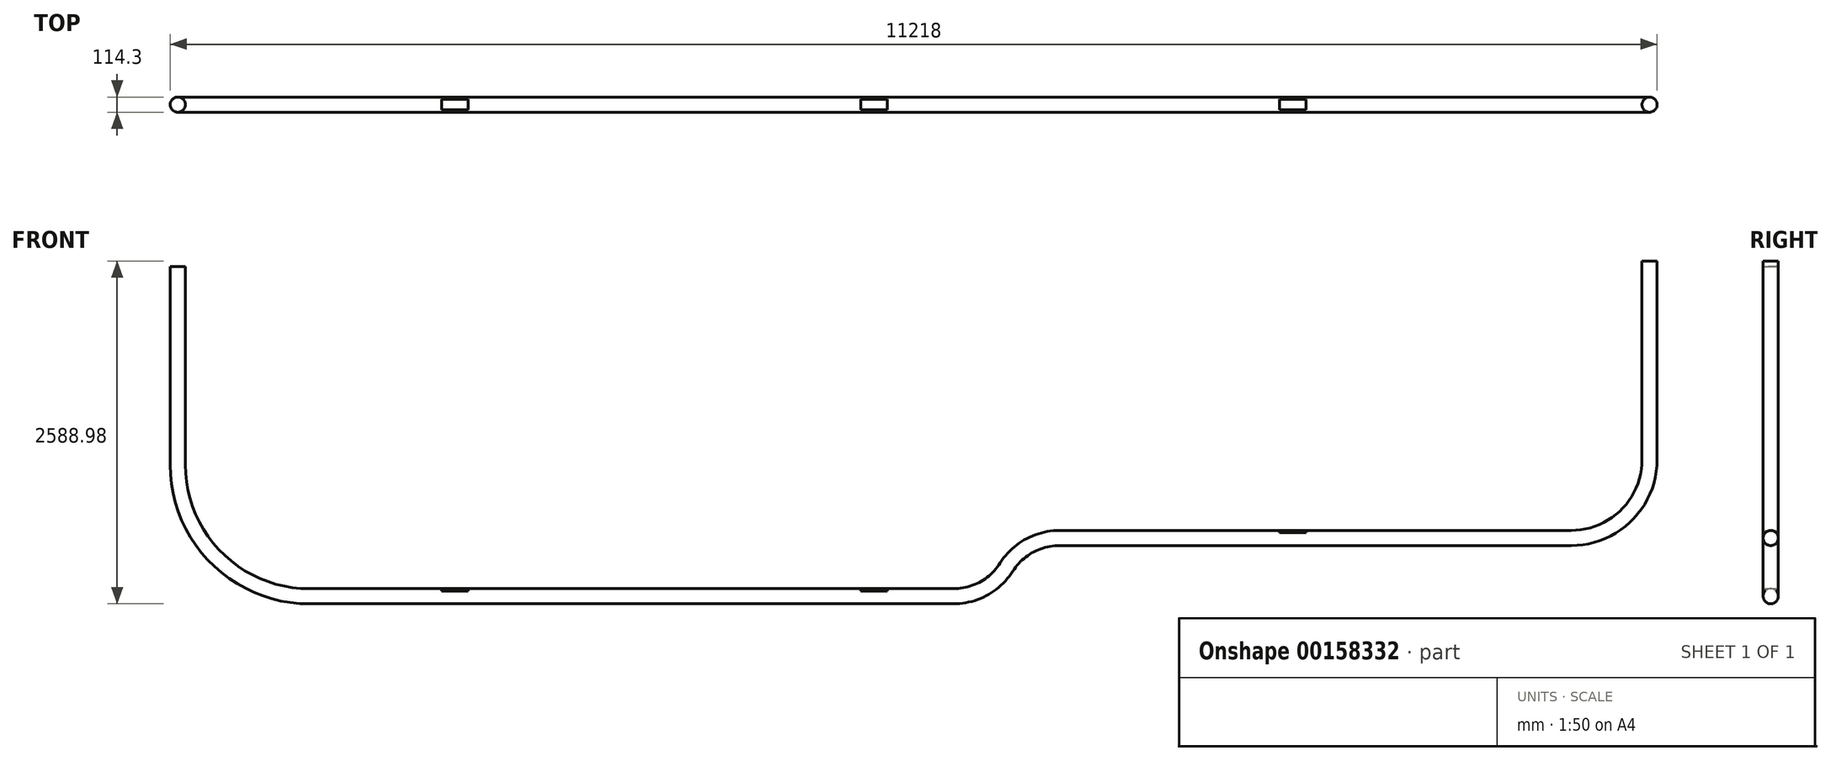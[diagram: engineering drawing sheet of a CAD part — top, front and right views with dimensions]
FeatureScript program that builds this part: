
annotation { "Feature Type Name" : "Feature", "Feature Type Description" : "" }
export const myFeature = defineFeature(function(context is Context, id is Id, definition is map)
    precondition{}
    {
        {
            var Q0;
            Q0=qCreatedBy(makeId("Right.planeOp"),FACE);
            var sketch = newSketch(context, id + "F0", { "sketchPlane" : qUnion([Q0])});
            skLineSegment(sketch, "E0", {"start": v(-40, 40.82) * mm, "end": v(-40, 57.15) * mm});
            skLineSegment(sketch, "E1", {"start": v(-40, 57.15) * mm, "end": v(40, 57.15) * mm});
            skLineSegment(sketch, "E2", {"start": v(40, 57.15) * mm, "end": v(40, 40.82) * mm});
            skArc(sketch, "E3", {"start": v(-40, 40.82) * mm, "mid": v(0, -57.15) * mm, "end": v(40, 40.82) * mm});
            skArc(sketch, "E4", {"start": v(40, 40.82) * mm, "mid": v(0, 57.15) * mm, "end": v(-40, 40.82) * mm, "construction": true});
            skPoint(sketch, "E5", {"position": v(0, 57.15) * mm});
            skSolve(sketch);
        }
        {
            var Q0;
            Q0 = qSketchRegion(id + "F0", true);
            extrude(context, id + "F1", {"entities" : qUnion([Q0]), "endBound" : BoundingType.SYMMETRIC, "depth" : 200 * mm});
        }
        {
            var Q0;
            Q0=makeQuery(id+"F1.opExtrude","CAP_FACE",FACE,{"disambiguationData":[OSD([sQuery(id+"F0.wireOp",EDGE,"E0"),sQuery(id+"F0.wireOp",EDGE,"E1"),sQuery(id+"F0.wireOp",EDGE,"E2"),sQuery(id+"F0.wireOp",EDGE,"E3")])],"isStart":false});
            var sketch = newSketch(context, id + "F2", { "sketchPlane" : qUnion([Q0])});
            skCircle(sketch, "E6", {"center": v(0, 0) * mm, "radius": 57.15 * mm});
            skSolve(sketch);
        }
        {
            var Q0;
            Q0=makeQuery(id+"F1.opExtrude","CAP_FACE",FACE,{"disambiguationData":[OSD([sQuery(id+"F0.wireOp",EDGE,"E0"),sQuery(id+"F0.wireOp",EDGE,"E1"),sQuery(id+"F0.wireOp",EDGE,"E2"),sQuery(id+"F0.wireOp",EDGE,"E3")])],"isStart":true});
            var sketch = newSketch(context, id + "F3", { "sketchPlane" : qUnion([Q0])});
            skCircle(sketch, "E7", {"center": v(0, 0) * mm, "radius": 57.15 * mm});
            skSolve(sketch);
        }
        {
            var Q0;
            Q0 = qSketchRegion(id + "F3", true);
            extrude(context, id + "F4", {"entities" : qUnion([Q0]), "operationType" : NewBodyOperationType.ADD, "depth" : 3160 * mm});
        }
        {
            var Q0;
            Q0=makeQuery(id+"F4.opExtrude","CAP_FACE",FACE,{"disambiguationData":[OSD([sQuery(id+"F3.wireOp",EDGE,"E7")])],"isStart":false});
            var sketch = newSketch(context, id + "F5", { "sketchPlane" : qUnion([Q0])});
            skLineSegment(sketch, "E8.0.0", {"start": v(-40, 57.15) * mm, "end": v(-40, 40.82) * mm});
            skArc(sketch, "E8.0.1", {"start": v(-40, 40.82) * mm, "mid": v(-21.6, 52.9) * mm, "end": v(0, 57.15) * mm});
            skLineSegment(sketch, "E8.0.2", {"start": v(0, 57.15) * mm, "end": v(-40, 57.15) * mm});
            skLineSegment(sketch, "E9.0.0", {"start": v(40, 57.15) * mm, "end": v(0, 57.15) * mm});
            skArc(sketch, "E9.0.1", {"start": v(0, 57.15) * mm, "mid": v(21.6, 52.9) * mm, "end": v(40, 40.82) * mm});
            skLineSegment(sketch, "E9.0.2", {"start": v(40, 40.82) * mm, "end": v(40, 57.15) * mm});
            skSolve(sketch);
        }
        {
            var Q0;
            Q0 = qSketchRegion(id + "F5", true);
            extrude(context, id + "F6", {"entities" : qUnion([Q0]), "operationType" : NewBodyOperationType.ADD, "oppositeDirection" : true, "depth" : 200 * mm});
        }
        {
            var Q0;
            Q0=qCreatedBy(makeId("Front.planeOp"),FACE);
            var sketch = newSketch(context, id + "F7", { "sketchPlane" : qUnion([Q0])});
            skLineSegment(sketch, "E10", {"start": v(100, 0) * mm, "end": v(600, 0) * mm});
            skArc(sketch, "E11", {"start": v(600, 0) * mm, "mid": v(828.25, 58.63) * mm, "end": v(1000, 220) * mm});
            skArc(sketch, "E12", {"start": v(1000, 220) * mm, "mid": v(1171.75, 381.37) * mm, "end": v(1400, 440) * mm});
            skLineSegment(sketch, "E13", {"start": v(1400, 440) * mm, "end": v(3260, 440) * mm});
            skSolve(sketch);
        }
        {
            var Q0;
            {var subQ0=sQuery(id+"F2.wireOp",EDGE,"E6");var subQ1=makeQuery(id+"F2.imprint","INTERSECT",VERTEX,{"derivedFrom":[makeQuery(id+"F1.opExtrude","CAP_EDGE",EDGE,{"disambiguationData":[OSD([sQuery(id+"F0.wireOp",EDGE,"E0")])],"isStart":false}),subQ0]});Q0=makeQuery(id+"F2.imprint","IMPRINT",FACE,{"disambiguationData":[TD([[makeQuery(id+"F2.imprint","IMPRINT",EDGE,{"disambiguationData":[TD([[subQ1,-1.0]])],"derivedFrom":subQ0}),1.0]])]});}
            var sketch = newSketch(context, id + "F8", { "sketchPlane" : qUnion([Q0])});
            skCircle(sketch, "E14", {"center": v(0, 0) * mm, "radius": 57.15 * mm});
            skSolve(sketch);
        }
        {
            var Q0;
            Q0 = qSketchRegion(id + "F8", true);
            var Q1;
            Q1 = qConstructionFilter(qBodyType(qCreatedBy(id + "F7" ,EDGE), BodyType.WIRE), ConstructionObject.NO);
            sweep(context, id + "F9", {"operationType" : NewBodyOperationType.ADD, "profiles" : qUnion([Q0]), "path" : qUnion([Q1])});
        }
        {
            var Q0;
            Q0=makeQuery(id+"F9.opSweep","CAP_FACE",FACE,{"disambiguationData":[OSD([sQuery(id+"F7.wireOp",VERTEX,"E13.end"),sQuery(id+"F8.wireOp",EDGE,"E14")])],"isStart":false});
            var sketch = newSketch(context, id + "F10", { "sketchPlane" : qUnion([Q0])});
            skLineSegment(sketch, "E15", {"start": v(-40, 480.82) * mm, "end": v(-40, 497.15) * mm});
            skLineSegment(sketch, "E16", {"start": v(-40, 497.15) * mm, "end": v(40, 497.15) * mm});
            skLineSegment(sketch, "E17", {"start": v(40, 497.15) * mm, "end": v(40, 480.82) * mm});
            skLineSegment(sketch, "E18", {"start": v(40, 480.82) * mm, "end": v(-40, 480.82) * mm});
            skSolve(sketch);
        }
        {
            var Q0;
            Q0 = qSketchRegion(id + "F10", true);
            extrude(context, id + "F11", {"entities" : qUnion([Q0]), "operationType" : NewBodyOperationType.ADD, "oppositeDirection" : true, "depth" : 200 * mm});
        }
        {
            var Q0;
            Q0=qCreatedBy(makeId("Front.planeOp"),FACE);
            var sketch = newSketch(context, id + "F12", { "sketchPlane" : qUnion([Q0])});
            skLineSegment(sketch, "E19", {"start": v(-3260, -8.17) * mm, "end": v(-4260, -8.17) * mm});
            skLineSegment(sketch, "E20.0", {"start": v(-3260, 40.82) * mm, "end": v(-3260, -57.15) * mm, "construction": true});
            skPoint(sketch, "E21", {"position": v(-3260, -8.17) * mm});
            skArc(sketch, "E22", {"start": v(-4260, -8.17) * mm, "mid": v(-4967.1, 284.73) * mm, "end": v(-5260, 991.83) * mm});
            skLineSegment(sketch, "E23", {"start": v(-5260, 991.83) * mm, "end": v(-5260, 2491.83) * mm});
            skSolve(sketch);
        }
        {
            var Q0;
            Q0=makeQuery(id+"F6.boolean.opBoolean","MERGE",FACE,{"derivedFrom":[makeQuery(id+"F4.opExtrude","CAP_FACE",FACE,{"disambiguationData":[OSD([sQuery(id+"F3.wireOp",EDGE,"E7")])],"isStart":false}),makeQuery(id+"F6.opExtrude","CAP_FACE",FACE,{"disambiguationData":[OSD([sQuery(id+"F5.wireOp",EDGE,"E8.0.0"),sQuery(id+"F5.wireOp",EDGE,"E8.0.1"),sQuery(id+"F5.wireOp",EDGE,"E8.0.2")])],"isStart":true}),makeQuery(id+"F6.opExtrude","CAP_FACE",FACE,{"disambiguationData":[OSD([sQuery(id+"F5.wireOp",EDGE,"E9.0.0"),sQuery(id+"F5.wireOp",EDGE,"E9.0.1"),sQuery(id+"F5.wireOp",EDGE,"E9.0.2")])],"isStart":true})]});
            var sketch = newSketch(context, id + "F13", { "sketchPlane" : qUnion([Q0])});
            skCircle(sketch, "E24", {"center": v(0, 0) * mm, "radius": 57.15 * mm});
            skSolve(sketch);
        }
        {
            var Q0;
            Q0 = qSketchRegion(id + "F13", true);
            var Q1;
            Q1 = qConstructionFilter(qBodyType(qCreatedBy(id + "F12" ,EDGE), BodyType.WIRE), ConstructionObject.NO);
            sweep(context, id + "F14", {"operationType" : NewBodyOperationType.ADD, "profiles" : qUnion([Q0]), "path" : qUnion([Q1])});
        }
        {
            var Q0;
            Q0=qCreatedBy(makeId("Front.planeOp"),FACE);
            var sketch = newSketch(context, id + "F15", { "sketchPlane" : qUnion([Q0])});
            skLineSegment(sketch, "E25", {"start": v(3260, 431.83) * mm, "end": v(5260, 431.83) * mm});
            skLineSegment(sketch, "E26.0", {"start": v(3260, 480.82) * mm, "end": v(3260, 382.85) * mm, "construction": true});
            skPoint(sketch, "E27", {"position": v(3260, 431.83) * mm});
            skArc(sketch, "E28", {"start": v(5260, 431.83) * mm, "mid": v(5684.26, 607.57) * mm, "end": v(5860, 1031.83) * mm});
            skLineSegment(sketch, "E29", {"start": v(5860, 1031.83) * mm, "end": v(5860, 2531.83) * mm});
            skSolve(sketch);
        }
        {
            var Q0;
            Q0=makeQuery(id+"F11.boolean.opBoolean","MERGE",FACE,{"derivedFrom":[makeQuery(id+"F9.opSweep","CAP_FACE",FACE,{"disambiguationData":[OSD([sQuery(id+"F7.wireOp",VERTEX,"E13.end"),sQuery(id+"F8.wireOp",EDGE,"E14")])],"isStart":false}),makeQuery(id+"F11.opExtrude","CAP_FACE",FACE,{"disambiguationData":[OSD([sQuery(id+"F10.wireOp",EDGE,"E15"),sQuery(id+"F10.wireOp",EDGE,"E16"),sQuery(id+"F10.wireOp",EDGE,"E17"),sQuery(id+"F10.wireOp",EDGE,"E18")])],"isStart":true})]});
            var sketch = newSketch(context, id + "F16", { "sketchPlane" : qUnion([Q0])});
            skCircle(sketch, "E30", {"center": v(0, 440) * mm, "radius": 57.15 * mm});
            skSolve(sketch);
        }
        {
            var Q0;
            Q0 = qSketchRegion(id + "F16", true);
            var Q1;
            Q1 = qConstructionFilter(qBodyType(qCreatedBy(id + "F15" ,EDGE), BodyType.WIRE), ConstructionObject.NO);
            sweep(context, id + "F17", {"operationType" : NewBodyOperationType.ADD, "profiles" : qUnion([Q0]), "path" : qUnion([Q1])});
        }
    });
